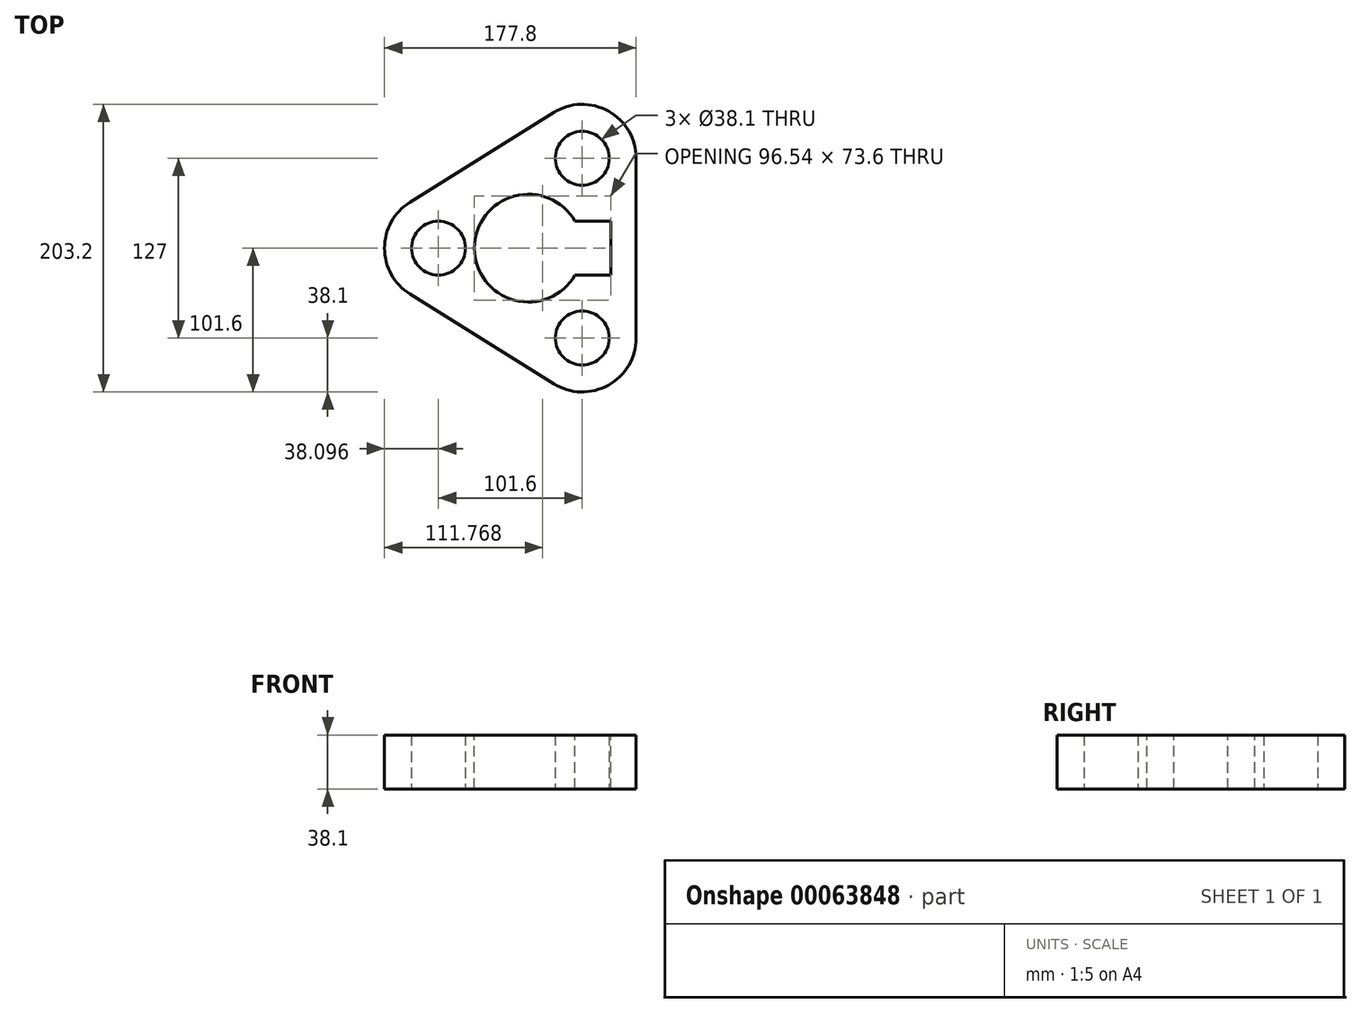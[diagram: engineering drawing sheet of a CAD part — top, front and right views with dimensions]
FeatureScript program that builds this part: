
annotation { "Feature Type Name" : "Feature", "Feature Type Description" : "" }
export const myFeature = defineFeature(function(context is Context, id is Id, definition is map)
    precondition{}
    {
        {
            var Q0;
            Q0=qCreatedBy(makeId("Top.planeOp"),FACE);
            var sketch = newSketch(context, id + "F0", { "sketchPlane" : qUnion([Q0])});
            skPoint(sketch, "E0.rect.middle", {"position": v(0, 0) * mm});
            skArc(sketch, "E1", {"start": v(-173.5, 32.3) * mm, "mid": v(-191.41, 0) * mm, "end": v(-173.5, -32.3) * mm});
            skArc(sketch, "E2", {"start": v(-13.61, 63.5) * mm, "mid": v(-33.24, 96.82) * mm, "end": v(-71.9, 95.8) * mm});
            skArc(sketch, "E3", {"start": v(-71.9, -95.8) * mm, "mid": v(-33.24, -96.82) * mm, "end": v(-13.61, -63.5) * mm});
            skLineSegment(sketch, "E4", {"start": v(-71.9, 95.8) * mm, "end": v(-173.5, 32.3) * mm});
            skLineSegment(sketch, "E5", {"start": v(-13.61, 63.5) * mm, "end": v(-13.61, -63.5) * mm});
            skLineSegment(sketch, "E6", {"start": v(-71.9, -95.8) * mm, "end": v(-173.5, -32.3) * mm});
            skCircle(sketch, "E7", {"center": v(-153.31, 0) * mm, "radius": 19.05 * mm});
            skCircle(sketch, "E8", {"center": v(-51.71, 63.5) * mm, "radius": 19.05 * mm});
            skCircle(sketch, "E9", {"center": v(-51.71, -63.5) * mm, "radius": 19.05 * mm});
            skSolve(sketch);
        }
        {
            var Q0;
            Q0=makeQuery(id+"F0.imprint","IMPRINT",FACE,{"disambiguationData":[TD([[makeQuery(id+"F0.imprint","IMPRINT",EDGE,{"derivedFrom":sQuery(id+"F0.wireOp",EDGE,"E1")}),1.0]])]});
            extrude(context, id + "F1", {"entities" : qUnion([Q0]), "depth" : 38.1 * mm});
        }
        {
            var Q0;
            Q0=makeQuery(id+"F1.opExtrude","CAP_FACE",FACE,{"disambiguationData":[OSD([sQuery(id+"F0.wireOp",EDGE,"E1"),sQuery(id+"F0.wireOp",EDGE,"E2"),sQuery(id+"F0.wireOp",EDGE,"E3"),sQuery(id+"F0.wireOp",EDGE,"E4"),sQuery(id+"F0.wireOp",EDGE,"E5"),sQuery(id+"F0.wireOp",EDGE,"E6"),sQuery(id+"F0.wireOp",EDGE,"E7"),sQuery(id+"F0.wireOp",EDGE,"E8"),sQuery(id+"F0.wireOp",EDGE,"E9")])],"isStart":false});
            var sketch = newSketch(context, id + "F2", { "sketchPlane" : qUnion([Q0])});
            skArc(sketch, "E10", {"start": v(-56.82, 19.05) * mm, "mid": v(-127.91, 0) * mm, "end": v(-56.82, -19.05) * mm});
            skPoint(sketch, "E11", {"position": v(-51.71, 63.5) * mm});
            skPoint(sketch, "E12", {"position": v(-153.31, 0) * mm});
            skPoint(sketch, "E13", {"position": v(-51.71, -63.5) * mm});
            skLineSegment(sketch, "E14.bottom", {"start": v(-56.82, 19.05) * mm, "end": v(-31.37, 19.05) * mm});
            skLineSegment(sketch, "E14.top", {"start": v(-56.82, -19.05) * mm, "end": v(-31.42, -19.05) * mm});
            skLineSegment(sketch, "E14.right", {"start": v(-31.37, 19.05) * mm, "end": v(-31.42, -19.05) * mm});
            skSolve(sketch);
        }
        {
            var Q0;
            Q0=makeQuery(id+"F2.imprint","IMPRINT",FACE,{"disambiguationData":[TD([[makeQuery(id+"F2.imprint","IMPRINT",EDGE,{"derivedFrom":sQuery(id+"F2.wireOp",EDGE,"E10")}),1.0]])]});
            extrude(context, id + "F3", {"entities" : qUnion([Q0]), "operationType" : NewBodyOperationType.REMOVE, "endBound" : BoundingType.THROUGH_ALL, "oppositeDirection" : true, "depth" : 25.4 * mm});
        }
    });
